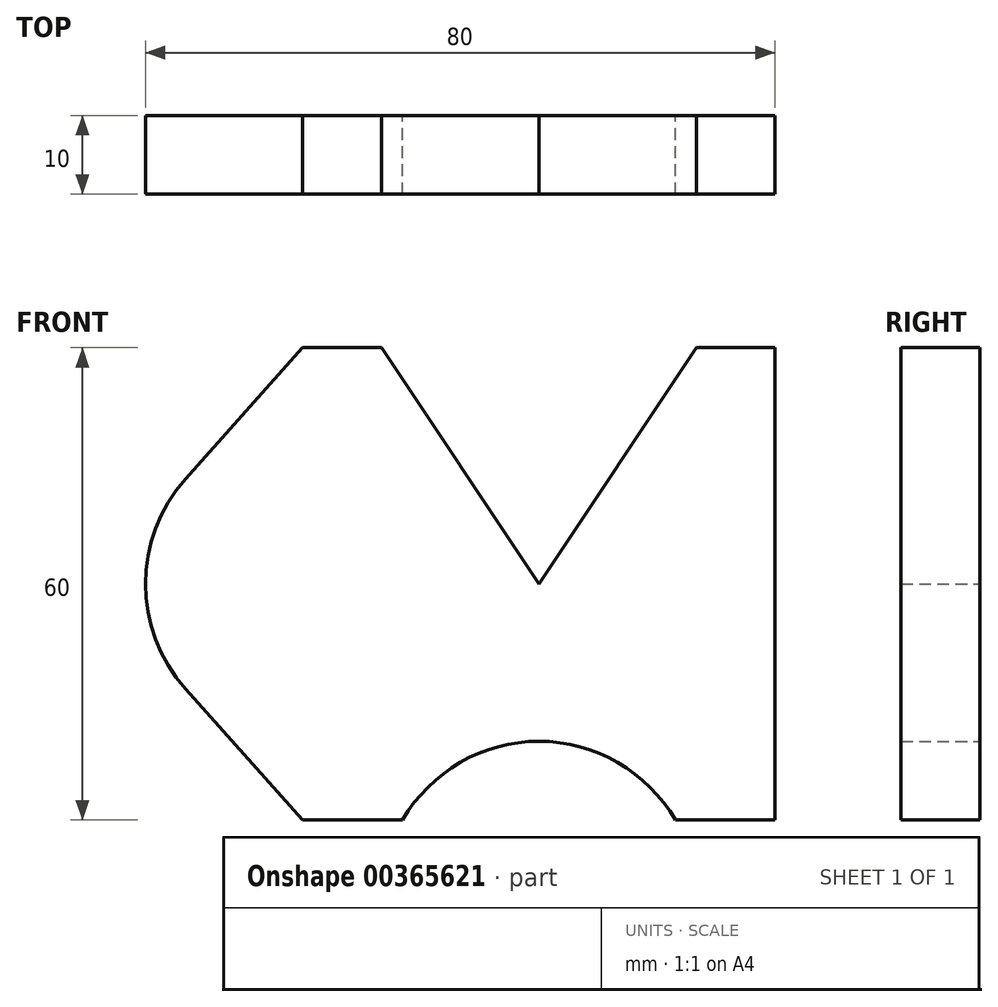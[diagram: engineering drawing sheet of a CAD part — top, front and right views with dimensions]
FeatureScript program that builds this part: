
annotation { "Feature Type Name" : "Feature", "Feature Type Description" : "" }
export const myFeature = defineFeature(function(context is Context, id is Id, definition is map)
    precondition{}
    {
        {
            var Q0;
            Q0=qCreatedBy(makeId("Front.planeOp"),FACE);
            var sketch = newSketch(context, id + "F0", { "sketchPlane" : qUnion([Q0])});
            skLineSegment(sketch, "E0", {"start": v(0, 0) * mm, "end": v(20, 30) * mm});
            skLineSegment(sketch, "E1", {"start": v(20, 30) * mm, "end": v(30, 30) * mm});
            skLineSegment(sketch, "E2", {"start": v(30, 30) * mm, "end": v(30, -30) * mm});
            skLineSegment(sketch, "E3", {"start": v(30, -30) * mm, "end": v(17.32, -30) * mm});
            skArc(sketch, "E4", {"start": v(17.32, -30) * mm, "mid": v(0, -20) * mm, "end": v(-17.32, -30) * mm});
            skLineSegment(sketch, "E5", {"start": v(-17.32, -30) * mm, "end": v(-30, -30) * mm});
            skLineSegment(sketch, "E6", {"start": v(-30, -30) * mm, "end": v(-44.9, -13.33) * mm});
            skArc(sketch, "E7", {"start": v(-44.9, 13.33) * mm, "mid": v(-50, 0) * mm, "end": v(-44.9, -13.33) * mm});
            skLineSegment(sketch, "E8", {"start": v(-44.9, 13.33) * mm, "end": v(-30, 30) * mm});
            skLineSegment(sketch, "E9", {"start": v(-30, 30) * mm, "end": v(-20, 30) * mm});
            skLineSegment(sketch, "E10", {"start": v(-20, 30) * mm, "end": v(0, 0) * mm});
            skLineSegment(sketch, "E11", {"start": v(-30, 41.46) * mm, "end": v(-30, -50.19) * mm, "construction": true});
            skSolve(sketch);
        }
        {
            var Q0;
            Q0=makeQuery(id+"F0.imprint","IMPRINT",FACE,{"disambiguationData":[TD([[makeQuery(id+"F0.imprint","IMPRINT",EDGE,{"derivedFrom":sQuery(id+"F0.wireOp",EDGE,"E0")}),-1.0]])]});
            extrude(context, id + "F1", {"entities" : qUnion([Q0]), "depth" : 10 * mm});
        }
    });
